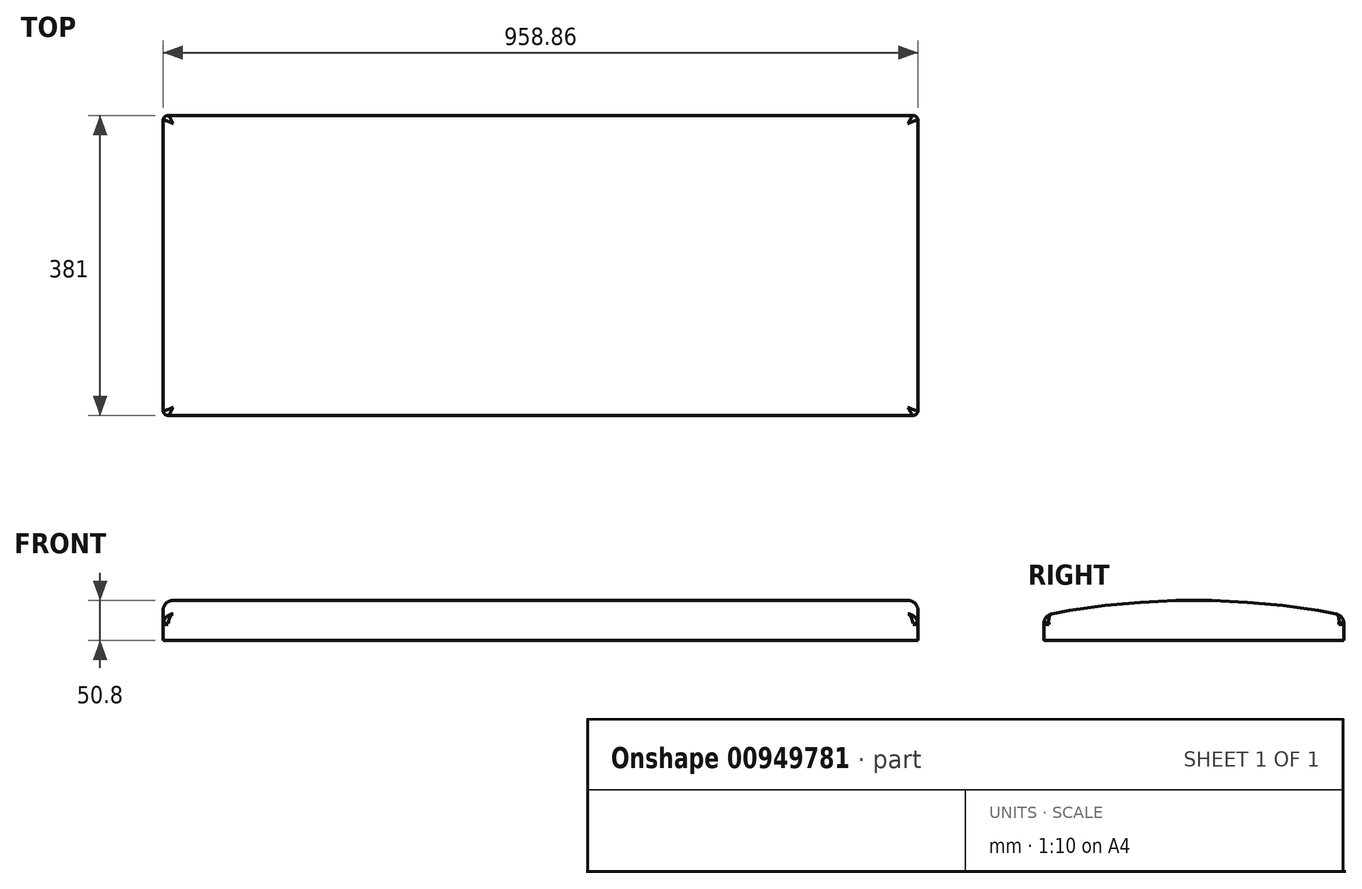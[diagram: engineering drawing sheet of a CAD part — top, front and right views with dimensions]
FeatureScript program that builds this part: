
annotation { "Feature Type Name" : "Feature", "Feature Type Description" : "" }
export const myFeature = defineFeature(function(context is Context, id is Id, definition is map)
    precondition{}
    {
        {
            var Q0;
            Q0=qCreatedBy(makeId("Right.planeOp"),FACE);
            var sketch = newSketch(context, id + "F0", { "sketchPlane" : qUnion([Q0])});
            skLineSegment(sketch, "E0.bottom", {"start": v(0, 0) * mm, "end": v(-381, 0) * mm});
            skLineSegment(sketch, "E0.left", {"start": v(0, 0) * mm, "end": v(0, 31.75) * mm});
            skLineSegment(sketch, "E0.right", {"start": v(-381, 0) * mm, "end": v(-381, 31.75) * mm});
            skArc(sketch, "E1", {"start": v(0, 31.75) * mm, "mid": v(-190.5, 50.8) * mm, "end": v(-381, 31.75) * mm});
            skPoint(sketch, "E2", {"position": v(-190.5, 50.8) * mm});
            skSolve(sketch);
        }
        {
            var Q0;
            Q0 = qSketchRegion(id + "F0", true);
            extrude(context, id + "F1", {"entities" : qUnion([Q0]), "endBound" : BoundingType.SYMMETRIC, "depth" : 958.85 * mm, "offsetDistance" : 25.4 * mm});
        }
        {
            var Q0;
            Q0=makeQuery(id+"F1.opExtrude","CAP_EDGE",EDGE,{"disambiguationData":[OSD([sQuery(id+"F0.wireOp",EDGE,"E0.right")])],"isStart":true});
            var Q1;
            Q1=makeQuery(id+"F1.opExtrude","CAP_EDGE",EDGE,{"disambiguationData":[OSD([sQuery(id+"F0.wireOp",EDGE,"E0.left")])],"isStart":true});
            var Q2;
            Q2=makeQuery(id+"F1.opExtrude","CAP_EDGE",EDGE,{"disambiguationData":[OSD([sQuery(id+"F0.wireOp",EDGE,"E0.left")])],"isStart":false});
            var Q3;
            Q3=makeQuery(id+"F1.opExtrude","CAP_EDGE",EDGE,{"disambiguationData":[OSD([sQuery(id+"F0.wireOp",EDGE,"E0.right")])],"isStart":false});
            fillet(context, id + "F2", {"entities" : qUnion([Q0, Q1, Q2, Q3]), "radius" : 6.35 * mm, "tangentPropagation" : true, "allowEdgeOverflow" : false});
        }
        {
            var Q0;
            Q0=makeQuery(id+"F1.opExtrude","CAP_EDGE",EDGE,{"disambiguationData":[OSD([sQuery(id+"F0.wireOp",EDGE,"E1")])],"isStart":false});
            fillet(context, id + "F3", {"entities" : qUnion([Q0]), "radius" : 12.7 * mm, "tangentPropagation" : true, "allowEdgeOverflow" : false});
        }
    });
